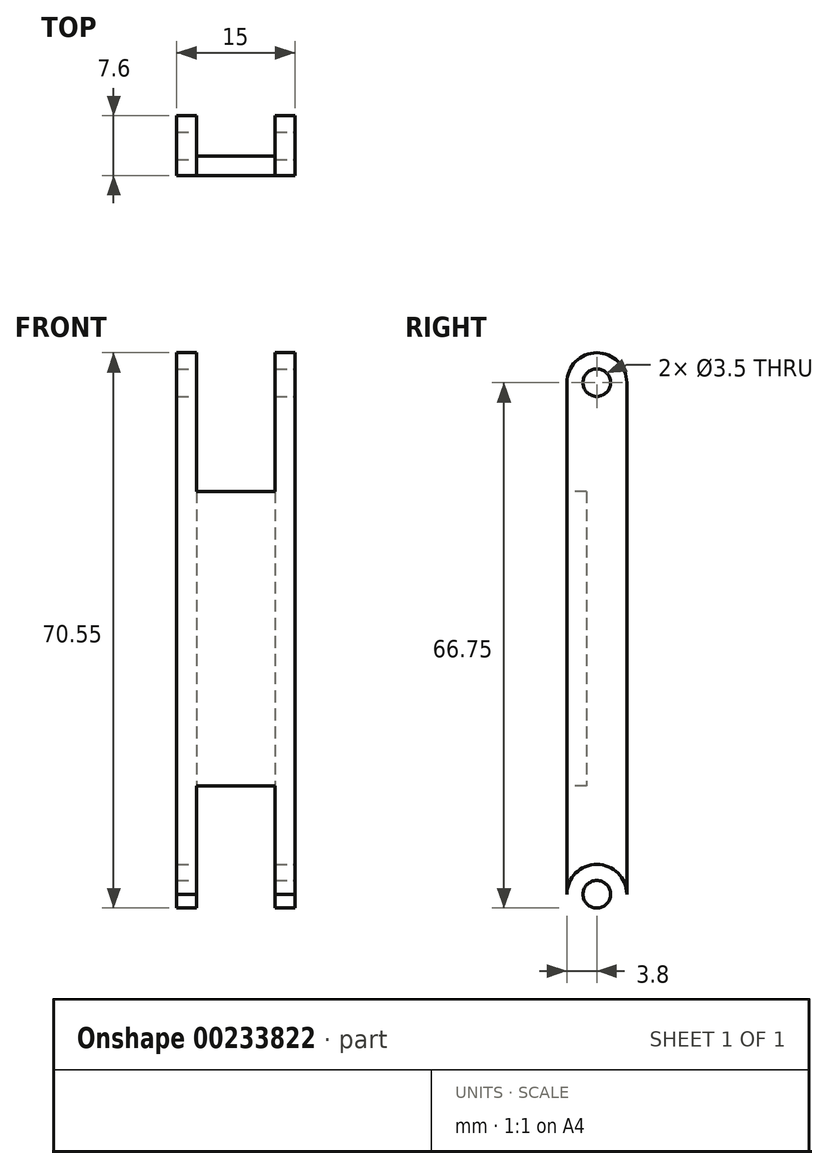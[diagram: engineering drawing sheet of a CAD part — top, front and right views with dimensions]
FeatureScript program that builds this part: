
annotation { "Feature Type Name" : "Feature", "Feature Type Description" : "" }
export const myFeature = defineFeature(function(context is Context, id is Id, definition is map)
    precondition{}
    {
        {
            var Q0;
            Q0=qCreatedBy(makeId("Top.planeOp"),FACE);
            var sketch = newSketch(context, id + "F0", { "sketchPlane" : qUnion([Q0])});
            skLineSegment(sketch, "E0.bottom", {"start": v(-7.5, 7.6) * mm, "end": v(-5, 7.6) * mm});
            skLineSegment(sketch, "E0.top", {"start": v(-7.5, 0) * mm, "end": v(-5, 0) * mm});
            skLineSegment(sketch, "E0.left", {"start": v(-7.5, 7.6) * mm, "end": v(-7.5, 0) * mm});
            skLineSegment(sketch, "E0.right", {"start": v(-5, 7.6) * mm, "end": v(-5, 0) * mm});
            skLineSegment(sketch, "E1.bottom", {"start": v(-5, 2.5) * mm, "end": v(0, 2.5) * mm});
            skLineSegment(sketch, "E1.top", {"start": v(-5, 0) * mm, "end": v(0, 0) * mm});
            skLineSegment(sketch, "E1.left", {"start": v(-5, 2.5) * mm, "end": v(-5, 0) * mm});
            skLineSegment(sketch, "E1.right", {"start": v(0, 2.5) * mm, "end": v(0, 0) * mm});
            skLineSegment(sketch, "E2.MirrorCS", {"start": v(5, 7.6) * mm, "end": v(5, 0) * mm});
            skLineSegment(sketch, "E3.MirrorCS", {"start": v(7.5, 7.6) * mm, "end": v(7.5, 0) * mm});
            skLineSegment(sketch, "E4.MirrorCS", {"start": v(7.5, 7.6) * mm, "end": v(5, 7.6) * mm});
            skLineSegment(sketch, "E5.MirrorCS", {"start": v(5, 0) * mm, "end": v(0, 0) * mm});
            skLineSegment(sketch, "E6.MirrorCS", {"start": v(5, 2.5) * mm, "end": v(0, 2.5) * mm});
            skLineSegment(sketch, "E7.MirrorCS", {"start": v(7.5, 0) * mm, "end": v(5, 0) * mm});
            skSolve(sketch);
        }
        {
            var Q0;
            Q0=makeQuery(id+"F0.imprint","IMPRINT",FACE,{"disambiguationData":[TD([[makeQuery(id+"F0.imprint","IMPRINT",EDGE,{"derivedFrom":sQuery(id+"F0.wireOp",EDGE,"E1.right")}),1.0]])]});
            var Q1;
            Q1=makeQuery(id+"F0.imprint","IMPRINT",FACE,{"disambiguationData":[TD([[makeQuery(id+"F0.imprint","IMPRINT",EDGE,{"derivedFrom":sQuery(id+"F0.wireOp",EDGE,"E1.bottom")}),-1.0]])]});
            extrude(context, id + "F1", {"entities" : qUnion([Q0, Q1]), "endBound" : BoundingType.SYMMETRIC, "depth" : 37.4 * mm});
        }
        {
            var Q0;
            Q0=makeQuery(id+"F0.imprint","IMPRINT",FACE,{"disambiguationData":[TD([[makeQuery(id+"F0.imprint","IMPRINT",EDGE,{"derivedFrom":sQuery(id+"F0.wireOp",EDGE,"E3.MirrorCS")}),-1.0]])]});
            var Q1;
            Q1=makeQuery(id+"F0.imprint","IMPRINT",FACE,{"disambiguationData":[TD([[makeQuery(id+"F0.imprint","IMPRINT",EDGE,{"derivedFrom":sQuery(id+"F0.wireOp",EDGE,"E0.bottom")}),-1.0]])]});
            extrude(context, id + "F2", {"entities" : qUnion([Q0, Q1]), "operationType" : NewBodyOperationType.ADD, "endBound" : BoundingType.SYMMETRIC, "depth" : 72.6 * mm});
        }
        {
            var Q0;
            Q0=makeQuery(id+"F2.opExtrude","SWEPT_FACE",FACE,{"disambiguationData":[OSD([sQuery(id+"F0.wireOp",EDGE,"E3.MirrorCS")])]});
            var sketch = newSketch(context, id + "F3", { "sketchPlane" : qUnion([Q0])});
            skCircle(sketch, "E8", {"center": v(3.8, 32.5) * mm, "radius": 1.75 * mm});
            skPoint(sketch, "E8.centerSnap0", {"position": v(3.8, 36.3) * mm});
            skCircle(sketch, "E9", {"center": v(3.8, 32.5) * mm, "radius": 3.8 * mm});
            skLineSegment(sketch, "E10.0", {"start": v(7.6, 36.3) * mm, "end": v(7.6, 32.5) * mm});
            skLineSegment(sketch, "E11.0", {"start": v(0, 36.3) * mm, "end": v(0, 32.5) * mm});
            skPoint(sketch, "E12.orphan", {"position": v(7.6, -36.3) * mm});
            skPoint(sketch, "E13.orphan", {"position": v(0, -36.3) * mm});
            skLineSegment(sketch, "E14", {"start": v(7.6, 36.3) * mm, "end": v(7.6, 42.82) * mm});
            skLineSegment(sketch, "E15", {"start": v(7.6, 42.82) * mm, "end": v(0, 42.82) * mm});
            skLineSegment(sketch, "E16", {"start": v(0, 42.82) * mm, "end": v(0, 36.3) * mm});
            skLineSegment(sketch, "E17.MirrorCS", {"start": v(0, -42.82) * mm, "end": v(0, -36.3) * mm});
            skCircle(sketch, "E18.MirrorC", {"center": v(3.8, -32.5) * mm, "radius": 3.8 * mm});
            skLineSegment(sketch, "E19.MirrorCS", {"start": v(7.6, -36.3) * mm, "end": v(7.6, -42.82) * mm});
            skLineSegment(sketch, "E20.MirrorCS", {"start": v(0, -36.3) * mm, "end": v(0, -32.5) * mm});
            skLineSegment(sketch, "E21.MirrorCS", {"start": v(7.6, -36.3) * mm, "end": v(7.6, -32.5) * mm});
            skLineSegment(sketch, "E22.MirrorCS", {"start": v(7.6, -42.82) * mm, "end": v(0, -42.82) * mm});
            skPoint(sketch, "E23.MirrorP", {"position": v(3.8, -36.3) * mm});
            skCircle(sketch, "E24.MirrorC", {"center": v(3.8, -32.5) * mm, "radius": 1.75 * mm});
            skSolve(sketch);
        }
        {
            var Q0;
            Q0=makeQuery(id+"F3.imprint","IMPRINT",FACE,{"disambiguationData":[TD([[makeQuery(id+"F3.imprint","IMPRINT",EDGE,{"derivedFrom":sQuery(id+"F3.wireOp",EDGE,"E8")}),1.0]])]});
            var Q1;
            {var subQ0=sQuery(id+"F3.wireOp",EDGE,"E14");Q1=makeQuery(id+"F3.imprint","IMPRINT",FACE,{"disambiguationData":[TD([[makeQuery(id+"F3.imprint","IMPRINT",EDGE,{"derivedFrom":subQ0}),1.0]])]});}
            var Q2;
            {var subQ0=sQuery(id+"F3.wireOp",EDGE,"E10.0");Q2=makeQuery(id+"F3.imprint","IMPRINT",FACE,{"disambiguationData":[TD([[makeQuery(id+"F3.imprint","IMPRINT",EDGE,{"derivedFrom":subQ0}),-1.0]])]});}
            var Q3;
            {var subQ0=sQuery(id+"F3.wireOp",EDGE,"E11.0");Q3=makeQuery(id+"F3.imprint","IMPRINT",FACE,{"disambiguationData":[TD([[makeQuery(id+"F3.imprint","IMPRINT",EDGE,{"derivedFrom":subQ0}),1.0]])]});}
            var Q4;
            Q4=makeQuery(id+"F3.imprint","IMPRINT",FACE,{"disambiguationData":[TD([[makeQuery(id+"F3.imprint","IMPRINT",EDGE,{"derivedFrom":sQuery(id+"F3.wireOp",EDGE,"E24.MirrorC")}),-1.0]])]});
            var Q5;
            {var subQ3=sQuery(id+"F3.wireOp",EDGE,"E17.MirrorCS");Q5=makeQuery(id+"F3.imprint","IMPRINT",FACE,{"disambiguationData":[TD([[makeQuery(id+"F3.imprint","IMPRINT",EDGE,{"derivedFrom":subQ3}),-1.0]])]});}
            var Q6;
            {var subQ0=sQuery(id+"F3.wireOp",EDGE,"E21.MirrorCS");Q6=makeQuery(id+"F3.imprint","IMPRINT",FACE,{"disambiguationData":[TD([[makeQuery(id+"F3.imprint","IMPRINT",EDGE,{"derivedFrom":subQ0}),-1.0]])]});}
            var Q7;
            {var subQ0=sQuery(id+"F3.wireOp",EDGE,"E20.MirrorCS");Q7=makeQuery(id+"F3.imprint","IMPRINT",FACE,{"disambiguationData":[TD([[makeQuery(id+"F3.imprint","IMPRINT",EDGE,{"derivedFrom":subQ0}),1.0]])]});}
            extrude(context, id + "F4", {"entities" : qUnion([Q0, Q1, Q2, Q3, Q4, Q5, Q6, Q7]), "operationType" : NewBodyOperationType.REMOVE, "endBound" : BoundingType.THROUGH_ALL, "oppositeDirection" : true, "depth" : 25 * mm});
        }
    });
